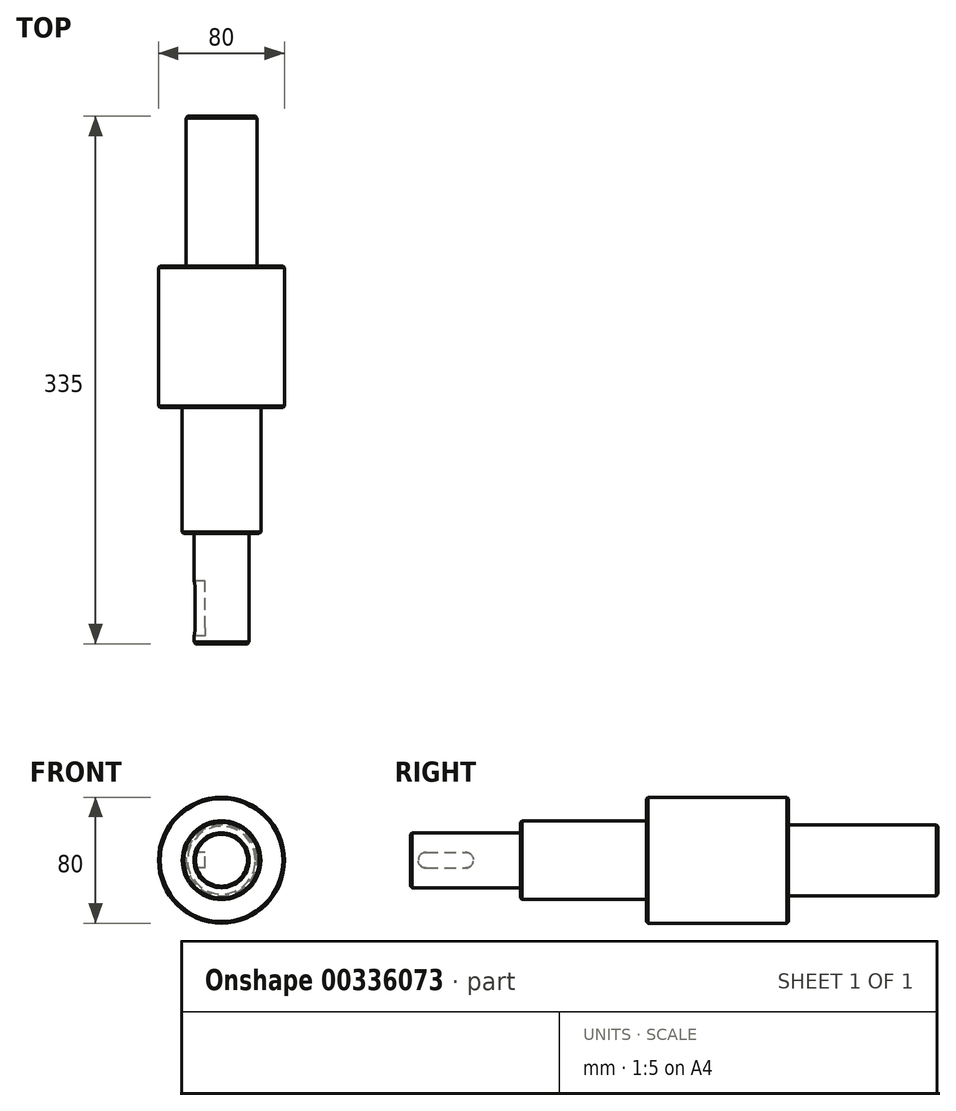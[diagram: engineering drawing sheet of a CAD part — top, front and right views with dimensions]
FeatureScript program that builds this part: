
annotation { "Feature Type Name" : "Feature", "Feature Type Description" : "" }
export const myFeature = defineFeature(function(context is Context, id is Id, definition is map)
    precondition{}
    {
        {
            var Q0;
            Q0=qCreatedBy(makeId("Front.planeOp"),FACE);
            var sketch = newSketch(context, id + "F0", { "sketchPlane" : qUnion([Q0])});
            skCircle(sketch, "E0", {"center": v(40.36, 0) * mm, "radius": 40 * mm});
            skSolve(sketch);
        }
        {
            var Q0;
            Q0 = qSketchRegion(id + "F0", true);
            extrude(context, id + "F1", {"entities" : qUnion([Q0]), "depth" : 90 * mm});
        }
        {
            var Q0;
            Q0=makeQuery(id+"F1.opExtrude","CAP_FACE",FACE,{"disambiguationData":[OSD([sQuery(id+"F0.wireOp",EDGE,"E0")])],"isStart":false});
            var sketch = newSketch(context, id + "F2", { "sketchPlane" : qUnion([Q0])});
            skCircle(sketch, "E1", {"center": v(40.36, 0) * mm, "radius": 25 * mm});
            skSolve(sketch);
        }
        {
            var Q0;
            Q0=makeQuery(id+"F2.imprint","IMPRINT",FACE,{"disambiguationData":[TD([[makeQuery(id+"F2.imprint","IMPRINT",EDGE,{"derivedFrom":sQuery(id+"F2.wireOp",EDGE,"E1")}),1.0]])]});
            extrude(context, id + "F3", {"entities" : qUnion([Q0]), "operationType" : NewBodyOperationType.ADD, "depth" : 80 * mm});
        }
        {
            var Q0;
            Q0=makeQuery(id+"F3.opExtrude","CAP_FACE",FACE,{"disambiguationData":[OSD([sQuery(id+"F2.wireOp",EDGE,"E1")])],"isStart":false});
            var sketch = newSketch(context, id + "F4", { "sketchPlane" : qUnion([Q0])});
            skCircle(sketch, "E2", {"center": v(40.36, 0) * mm, "radius": 17.5 * mm});
            skSolve(sketch);
        }
        {
            var Q0;
            Q0 = qSketchRegion(id + "F4", true);
            var Q1;
            Q1=makeQuery(id+"F4.imprint","IMPRINT",FACE,{"disambiguationData":[TD([[makeQuery(id+"F4.imprint","IMPRINT",EDGE,{"derivedFrom":sQuery(id+"F4.wireOp",EDGE,"E2")}),1.0]])]});
            extrude(context, id + "F5", {"entities" : qUnion([Q0, Q1]), "operationType" : NewBodyOperationType.ADD, "depth" : 70 * mm});
        }
        {
            var Q0;
            Q0=qCreatedBy(makeId("Right.planeOp"),FACE);
            var sketch = newSketch(context, id + "F6", { "sketchPlane" : qUnion([Q0])});
            skLineSegment(sketch, "E3.bottom", {"start": v(-230, -5) * mm, "end": v(-205, -5) * mm});
            skLineSegment(sketch, "E3.top", {"start": v(-230, 5) * mm, "end": v(-205, 5) * mm});
            skLineSegment(sketch, "E3.left", {"start": v(-230, -5) * mm, "end": v(-230, -5) * mm});
            skLineSegment(sketch, "E3.right", {"start": v(-205, -5) * mm, "end": v(-205, -5) * mm});
            skPoint(sketch, "E3.middle", {"position": v(-217.5, 0) * mm});
            skArc(sketch, "E4", {"start": v(-205, -5) * mm, "mid": v(-200, 0) * mm, "end": v(-205, 5) * mm});
            skArc(sketch, "E5", {"start": v(-230, 5) * mm, "mid": v(-235, 0) * mm, "end": v(-230, -5) * mm});
            skLineSegment(sketch, "E6.trimOffspring", {"start": v(-230, 5) * mm, "end": v(-230, 5) * mm});
            skLineSegment(sketch, "E7.trimOffspring", {"start": v(-205, 5) * mm, "end": v(-205, 5) * mm});
            skSolve(sketch);
        }
        {
            var Q0;
            Q0=makeQuery(id+"F6.imprint","IMPRINT",FACE,{"disambiguationData":[TD([[makeQuery(id+"F6.imprint","IMPRINT",EDGE,{"derivedFrom":sQuery(id+"F6.wireOp",EDGE,"E3.bottom")}),1.0]])]});
            extrude(context, id + "F7", {"entities" : qUnion([Q0]), "operationType" : NewBodyOperationType.REMOVE, "depth" : 30 * mm});
        }
        {
            var Q0;
            Q0=makeQuery(id+"F5.opExtrude","CAP_EDGE",EDGE,{"disambiguationData":[OSD([sQuery(id+"F4.wireOp",EDGE,"E2")])],"isStart":false});
            var Q1;
            Q1=makeQuery(id+"F3.opExtrude","CAP_EDGE",EDGE,{"disambiguationData":[OSD([sQuery(id+"F2.wireOp",EDGE,"E1")])],"isStart":false});
            var Q2;
            Q2=makeQuery(id+"F1.opExtrude","CAP_EDGE",EDGE,{"disambiguationData":[OSD([sQuery(id+"F0.wireOp",EDGE,"E0")])],"isStart":false});
            chamfer(context, id + "F8", {"entities" : qUnion([Q0, Q1, Q2]), "width" : 1 * mm, "tangentPropagation" : true});
        }
        {
            var Q0;
            Q0=makeQuery(id+"F1.opExtrude","CAP_FACE",FACE,{"disambiguationData":[OSD([sQuery(id+"F0.wireOp",EDGE,"E0")])],"isStart":true});
            var sketch = newSketch(context, id + "F9", { "sketchPlane" : qUnion([Q0])});
            skCircle(sketch, "E8", {"center": v(-40.36, 0) * mm, "radius": 22.5 * mm});
            skSolve(sketch);
        }
        {
            var Q0;
            Q0=makeQuery(id+"F9.imprint","IMPRINT",FACE,{"disambiguationData":[TD([[makeQuery(id+"F9.imprint","IMPRINT",EDGE,{"derivedFrom":sQuery(id+"F9.wireOp",EDGE,"E8")}),1.0]])]});
            extrude(context, id + "F10", {"entities" : qUnion([Q0]), "operationType" : NewBodyOperationType.ADD, "depth" : 95 * mm});
        }
        {
            var Q0;
            Q0=makeQuery(id+"F10.opExtrude","CAP_EDGE",EDGE,{"disambiguationData":[OSD([sQuery(id+"F9.wireOp",EDGE,"E8")])],"isStart":false});
            var Q1;
            Q1=makeQuery(id+"F1.opExtrude","CAP_EDGE",EDGE,{"disambiguationData":[OSD([sQuery(id+"F0.wireOp",EDGE,"E0")])],"isStart":true});
            chamfer(context, id + "F11", {"entities" : qUnion([Q0, Q1]), "width" : 1 * mm, "tangentPropagation" : true});
        }
    });
